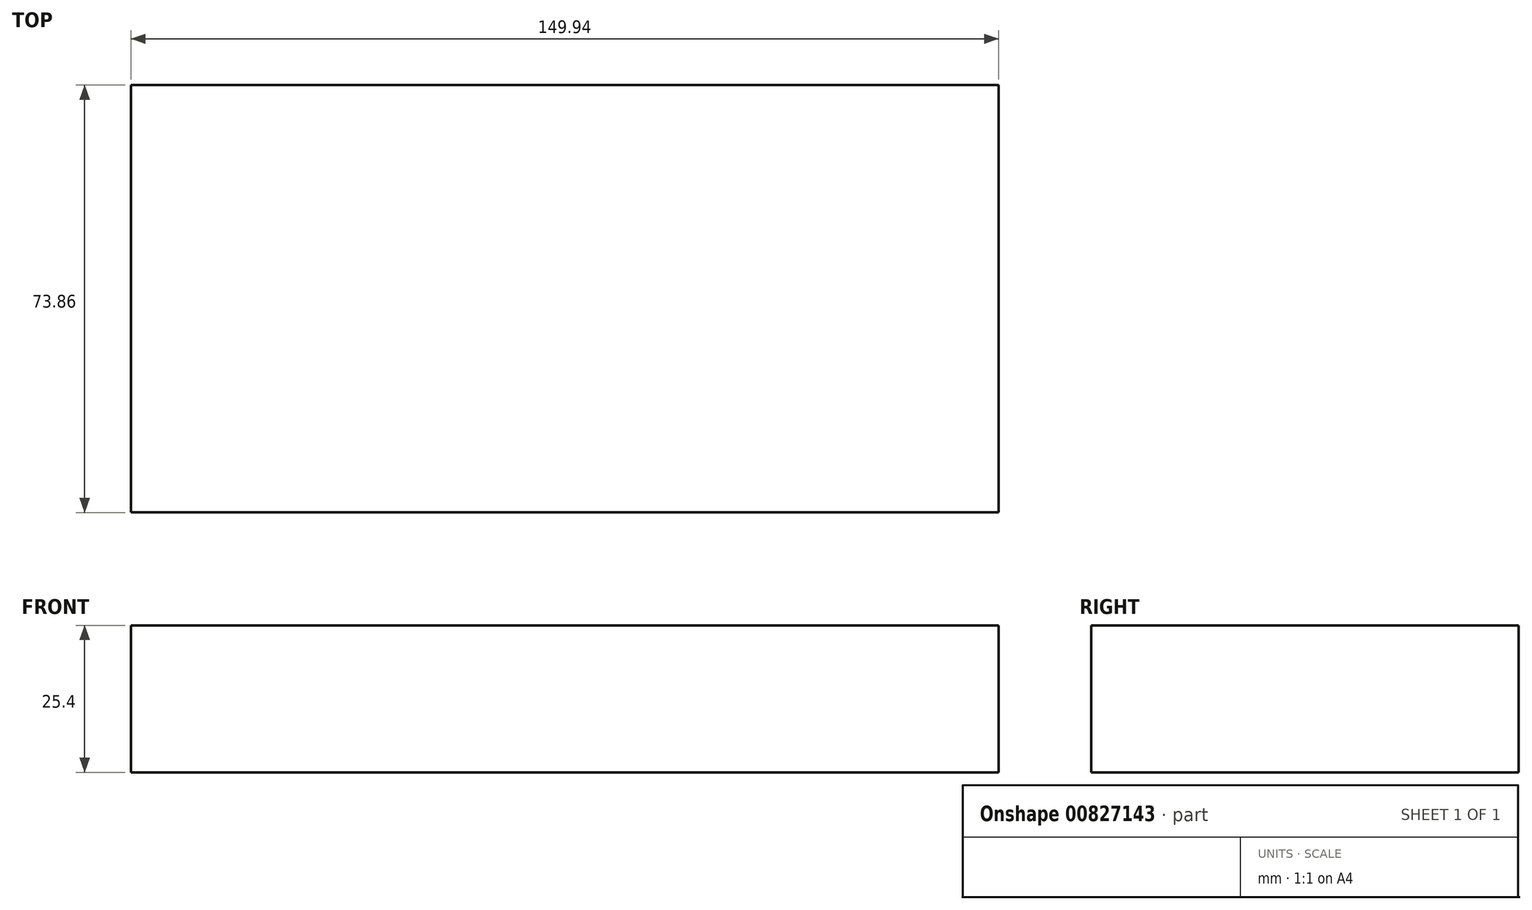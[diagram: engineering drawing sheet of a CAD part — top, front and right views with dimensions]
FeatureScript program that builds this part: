
annotation { "Feature Type Name" : "Feature", "Feature Type Description" : "" }
export const myFeature = defineFeature(function(context is Context, id is Id, definition is map)
    precondition{}
    {
        {
            var Q0;
            Q0=qCreatedBy(makeId("Top.planeOp"),FACE);
            var sketch = newSketch(context, id + "F0", { "sketchPlane" : qUnion([Q0])});
            skLineSegment(sketch, "E0.bottom", {"start": v(-95.87, 17.32) * mm, "end": v(54.07, 17.32) * mm});
            skLineSegment(sketch, "E0.top", {"start": v(-95.87, -56.54) * mm, "end": v(54.07, -56.54) * mm});
            skLineSegment(sketch, "E0.left", {"start": v(-95.87, 17.32) * mm, "end": v(-95.87, -56.54) * mm});
            skLineSegment(sketch, "E0.right", {"start": v(54.07, 17.32) * mm, "end": v(54.07, -56.54) * mm});
            skSolve(sketch);
        }
        {
            var Q0;
            Q0 = qSketchRegion(id + "F0", true);
            extrude(context, id + "F1", {"entities" : qUnion([Q0]), "depth" : 25.4 * mm, "offsetDistance" : 25.4 * mm});
        }
    });
